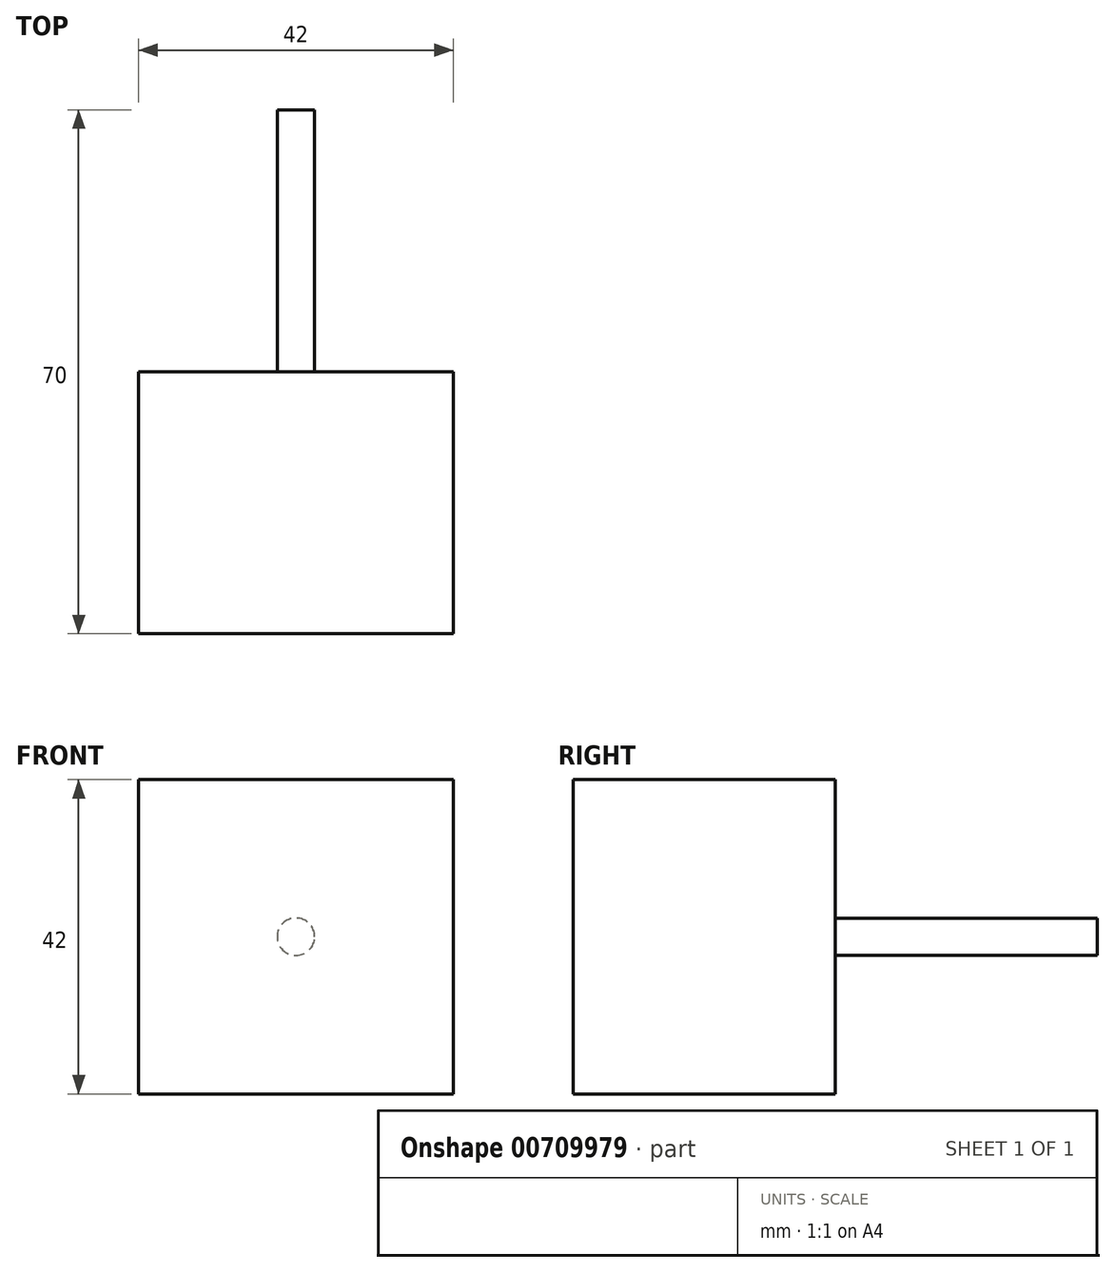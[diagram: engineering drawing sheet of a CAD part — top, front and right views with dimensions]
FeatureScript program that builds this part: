
annotation { "Feature Type Name" : "Feature", "Feature Type Description" : "" }
export const myFeature = defineFeature(function(context is Context, id is Id, definition is map)
    precondition{}
    {
        {
            var Q0;
            Q0=qCreatedBy(makeId("Front.planeOp"),FACE);
            var sketch = newSketch(context, id + "F0", { "sketchPlane" : qUnion([Q0])});
            skLineSegment(sketch, "E0.bottom", {"start": v(21, -21) * mm, "end": v(-21, -21) * mm});
            skLineSegment(sketch, "E0.top", {"start": v(21, 21) * mm, "end": v(-21, 21) * mm});
            skLineSegment(sketch, "E0.left", {"start": v(21, -21) * mm, "end": v(21, 21) * mm});
            skLineSegment(sketch, "E0.right", {"start": v(-21, -21) * mm, "end": v(-21, 21) * mm});
            skPoint(sketch, "E0.middle", {"position": v(0, 0) * mm});
            skCircle(sketch, "E1", {"center": v(0, 0) * mm, "radius": 2.5 * mm});
            skSolve(sketch);
        }
        {
            var Q0;
            Q0=makeQuery(id+"F0.imprint","IMPRINT",FACE,{"disambiguationData":[TD([[makeQuery(id+"F0.imprint","IMPRINT",EDGE,{"derivedFrom":sQuery(id+"F0.wireOp",EDGE,"E0.bottom")}),-1.0]])]});
            var Q1;
            Q1=makeQuery(id+"F0.imprint","IMPRINT",FACE,{"disambiguationData":[TD([[makeQuery(id+"F0.imprint","IMPRINT",EDGE,{"derivedFrom":sQuery(id+"F0.wireOp",EDGE,"E1")}),1.0]])]});
            extrude(context, id + "F1", {"entities" : qUnion([Q0, Q1]), "depth" : 35 * mm, "offsetDistance" : 25 * mm});
        }
        {
            var Q0;
            Q0=makeQuery(id+"F0.imprint","IMPRINT",FACE,{"disambiguationData":[TD([[makeQuery(id+"F0.imprint","IMPRINT",EDGE,{"derivedFrom":sQuery(id+"F0.wireOp",EDGE,"E1")}),1.0]])]});
            extrude(context, id + "F2", {"entities" : qUnion([Q0]), "operationType" : NewBodyOperationType.ADD, "oppositeDirection" : true, "depth" : 35 * mm, "offsetDistance" : 25 * mm});
        }
    });
